# Revit family: Doors_Swing_Hajom_Architect_Type-FDU
name_source: partatom
category: Doors
revit_build: Autodesk Revit 2018 (Build: 20170223_1515(x64)
units: mm (PartAtom-declared; Revit-internal decimal feet)

## family parameters
Always vertical = Yes
Cut with Voids When Loaded = No
Host = Wall
OmniClass Number = 23.30.10.00
OmniClass Title = Doors
Room Calculation Point = No
Shared = No

## types (1)
- Architect - Type FDU
    AssetType = Fixed
    BIMObjectName = Doors_Swing_Hajom_Architect_Type-FDU
    Brand = Hajom
    Category = Doors
    Default Sill Height = 0 mm  [stored 0 ft]
    DurationUnit = Year
    Height = 0 mm  [stored 0 ft]
    Manufacturer = Hajom
    ManufacturerName = Hajom
    ManufacturerURL = https://www.hajom.com
    Material = Wood
    Model = Architect - Type FDU
    NBSDescription = Wood doorsets
    NBSReference = 45-25-28/348
    Name = Architect_Type-FDU
    NominalDepth = 105 mm  [stored 0.344488 ft]
    Revision = 1
    Rough Height = 0 mm  [stored 0 ft]
    Rough Width = 0 mm  [stored 0 ft]
    Shape = Rectangular
    Size = 380-1080x380-1980x105 mm
    URL = https://www.hajom.com
    Uniclass2 = Pr_30_59_23_36
    Uniclass2015Description = Wood doorsets
    Uniclass2015Reference = Pr_30_59_24_97
    Version = 2
    VersionDate = 18/08/2022
    Wall Closure = By host
    WarrantyDurationUnit = Year
    Width = 0 mm  [stored 0 ft]

note: [stored X ft] marks values corroborated as IEEE doubles in the binary element streams (Revit-internal decimal feet)

## geometry (parser evidence)
native form markers: Sweep x40
no freeform markers — native parametric forms only
